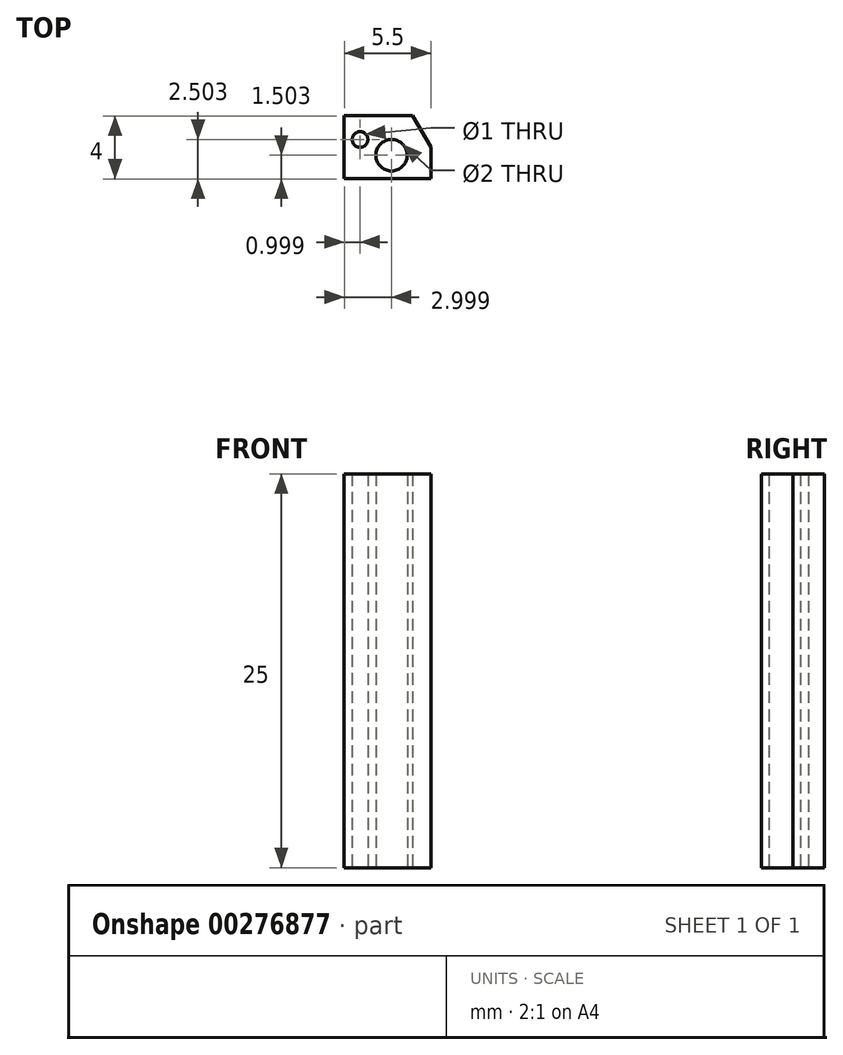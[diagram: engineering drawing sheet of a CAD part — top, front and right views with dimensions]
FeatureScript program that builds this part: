
annotation { "Feature Type Name" : "Feature", "Feature Type Description" : "" }
export const myFeature = defineFeature(function(context is Context, id is Id, definition is map)
    precondition{}
    {
        {
            var Q0;
            Q0=qCreatedBy(makeId("Top.planeOp"),FACE);
            var sketch = newSketch(context, id + "F0", { "sketchPlane" : qUnion([Q0])});
            skLineSegment(sketch, "E0", {"start": v(-55.27, 46.02) * mm, "end": v(-55.27, 44.02) * mm});
            skLineSegment(sketch, "E1", {"start": v(-55.27, 44.02) * mm, "end": v(-60.77, 44.02) * mm});
            skPoint(sketch, "E2.trimOffspring.end.orphan", {"position": v(-60.77, 48.02) * mm});
            skPoint(sketch, "E3.start.orphan", {"position": v(-55.27, 48.02) * mm});
            skLineSegment(sketch, "E4", {"start": v(-55.27, 44.02) * mm, "end": v(-55.27, 46.02) * mm});
            skLineSegment(sketch, "E5", {"start": v(-60.77, 48.02) * mm, "end": v(-60.77, 44.02) * mm});
            skPoint(sketch, "E6.end.orphan", {"position": v(-56.43, 48.02) * mm});
            skLineSegment(sketch, "E7", {"start": v(-56.43, 48.02) * mm, "end": v(-60.77, 48.02) * mm});
            skLineSegment(sketch, "E8", {"start": v(-56.43, 48.02) * mm, "end": v(-55.27, 46.02) * mm});
            skLineSegment(sketch, "E9", {"start": v(-60.77, 44.02) * mm, "end": v(-60.77, 46.52) * mm});
            skCircle(sketch, "E10", {"center": v(-59.77, 46.52) * mm, "radius": 0.5 * mm});
            skCircle(sketch, "E11", {"center": v(-57.77, 45.52) * mm, "radius": 0.5 * mm});
            skCircle(sketch, "E12", {"center": v(-57.77, 45.52) * mm, "radius": 1 * mm});
            skSolve(sketch);
        }
        {
            var Q0;
            Q0 = qSketchRegion(id + "F0", true);
            extrude(context, id + "F1", {"entities" : qUnion([Q0]), "depth" : 25 * mm});
        }
    });
